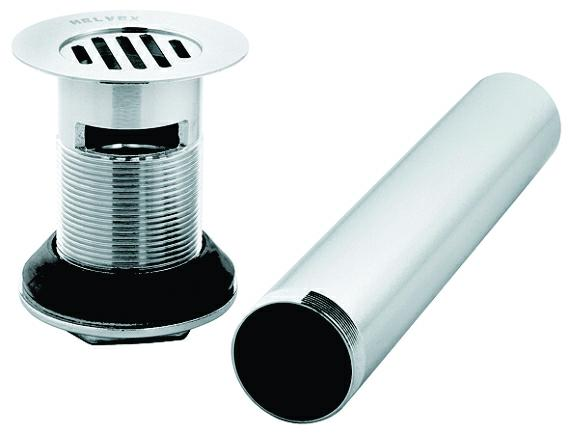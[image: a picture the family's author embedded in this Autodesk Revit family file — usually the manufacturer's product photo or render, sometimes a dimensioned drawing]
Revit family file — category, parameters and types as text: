
# Revit family: Contra de rejilla TH-058
name_source: partatom
category: Aparatos sanitarios
revit_build: Autodesk Revit 2016 (Build: 20150220_1215(x64)
units: mm (PartAtom-declared; Revit-internal decimal feet)

## family parameters
Compartido = Sí
Corte con vacíos al cargar = No
Cota de conector redondo = Diámetro de uso
Número OmniClass = 23.45.05.14.99
Punto de cálculo de habitación = Sí
Se basa en plano de trabajo = No
Siempre vertical = Sí
Tipo de pieza = Normal
Título OmniClass = Other Sanitary Washing Plumbing Fixtures

## types (1)
- TH-058
    Brass Chromed = Brass
    Comentarios de tipo = Lavatory Accesories
    Data Sheet = http://www.helvex.com.mx
    Descripción = Lavatory Grid Drain With Overflow
    Elevación por Defecto = 1"
    Fabricante = HELVEX
    Features = Fixed Grid; With Overflow
    Imagen de tipo = TH-058.jpg
    Inlet Threads = 1 ¼" Pipe
    Modelo = TH-058
    Total Diameter = 2"
    Total Height = 10"
    URL = http://www.helvex.com.mx

## geometry (parser evidence)
native form markers: Sweep x3
no freeform markers — native parametric forms only
